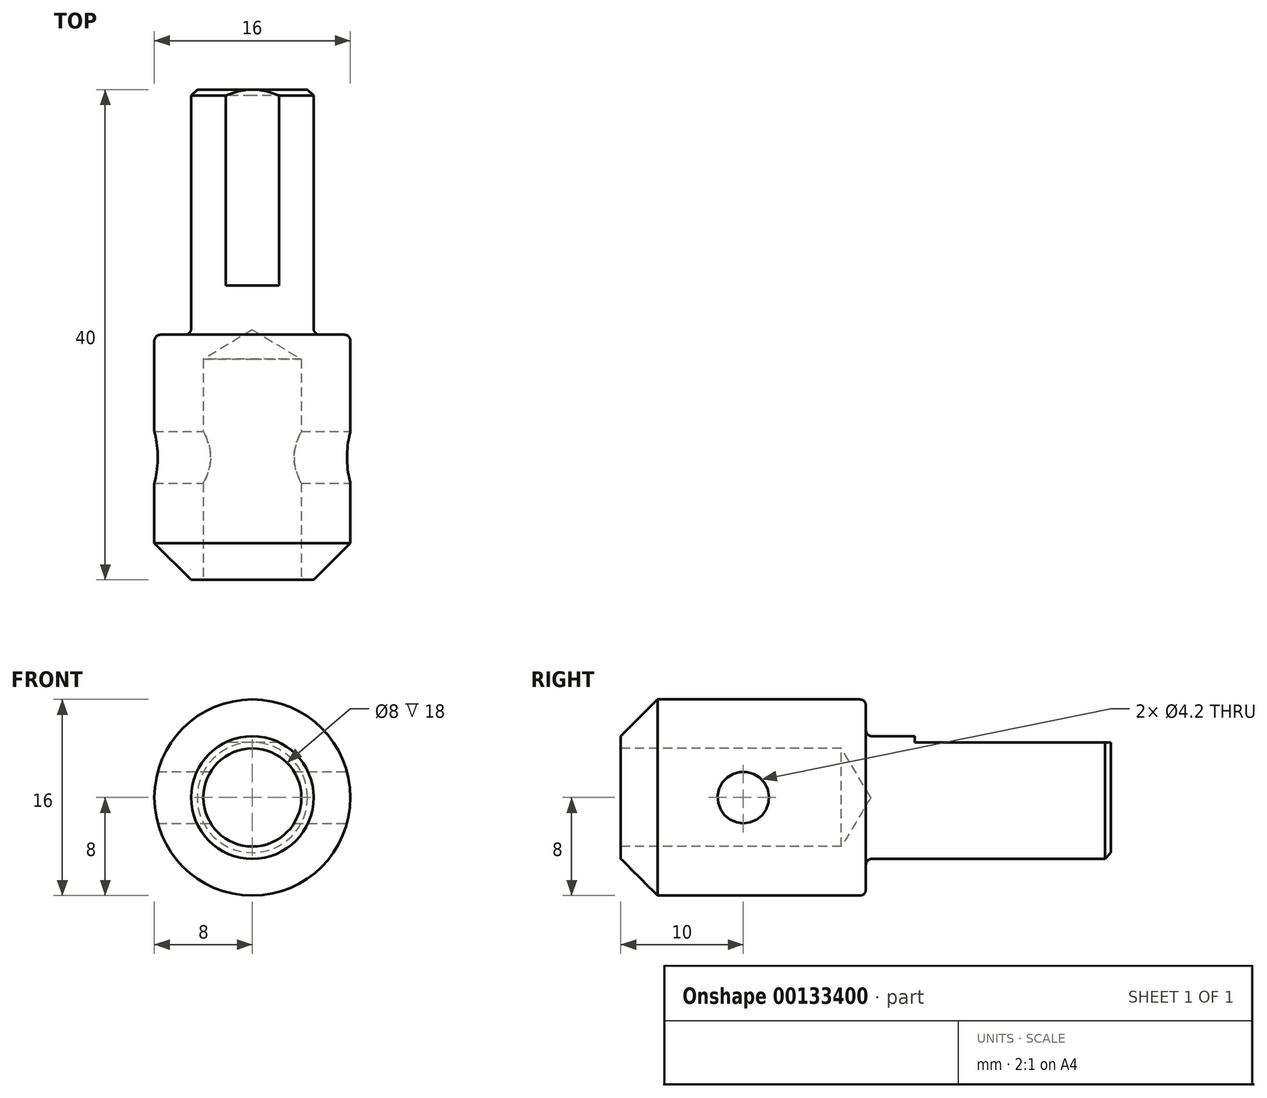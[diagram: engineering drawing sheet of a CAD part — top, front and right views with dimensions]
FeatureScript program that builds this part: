
annotation { "Feature Type Name" : "Feature", "Feature Type Description" : "" }
export const myFeature = defineFeature(function(context is Context, id is Id, definition is map)
    precondition{}
    {
        {
            var Q0;
            Q0=qCreatedBy(makeId("Front.planeOp"),FACE);
            var sketch = newSketch(context, id + "F0", { "sketchPlane" : qUnion([Q0])});
            skCircle(sketch, "E0", {"center": v(0, 0) * mm, "radius": 8 * mm});
            skSolve(sketch);
        }
        {
            var Q0;
            Q0=qSketchRegion(id+"F0",true);
            extrude(context, id + "F1", {"entities" : qUnion([Q0]), "oppositeDirection" : true, "depth" : 20 * mm});
        }
        {
            var Q0;
            Q0=makeQuery(id+"F1.opExtrude","CAP_FACE",FACE,{"disambiguationData":[OSD([sQuery(id+"F0.wireOp",EDGE,"E0")])],"isStart":false});
            var sketch = newSketch(context, id + "F2", { "sketchPlane" : qUnion([Q0])});
            skCircle(sketch, "E1", {"center": v(0, 0) * mm, "radius": 5 * mm});
            skSolve(sketch);
        }
        {
            var Q0;
            Q0=qSketchRegion(id+"F2",true);
            extrude(context, id + "F3", {"entities" : qUnion([Q0]), "operationType" : NewBodyOperationType.ADD, "depth" : 20 * mm});
        }
        {
            var Q0;
            Q0=makeQuery(id+"F3.opExtrude","CAP_FACE",FACE,{"disambiguationData":[OSD([sQuery(id+"F2.wireOp",EDGE,"E1")])],"isStart":false});
            var sketch = newSketch(context, id + "F4", { "sketchPlane" : qUnion([Q0])});
            skLineSegment(sketch, "E2", {"start": v(-2.18, 4.5) * mm, "end": v(2.18, 4.5) * mm});
            skArc(sketch, "E3", {"start": v(2.18, 4.5) * mm, "mid": v(0, 5) * mm, "end": v(-2.18, 4.5) * mm});
            skSolve(sketch);
        }
        {
            var Q0;
            Q0=qSketchRegion(id+"F4",true);
            extrude(context, id + "F5", {"entities" : qUnion([Q0]), "operationType" : NewBodyOperationType.REMOVE, "oppositeDirection" : true, "depth" : 16 * mm});
        }
        {
            var Q0;
            Q0=makeQuery(id+"F3.opExtrude","CAP_EDGE",EDGE,{"disambiguationData":[OSD([sQuery(id+"F2.wireOp",EDGE,"E1")])],"isStart":false});
            chamfer(context, id + "F6", {"entities" : qUnion([Q0]), "width" : .5 * mm, "tangentPropagation" : true});
        }
        {
            var Q0;
            Q0=makeQuery(id+"F1.opExtrude","CAP_FACE",FACE,{"disambiguationData":[OSD([sQuery(id+"F0.wireOp",EDGE,"E0")])],"isStart":false});
            fillet(context, id + "F7", {"entities" : qUnion([Q0]), "radius" : .5 * mm, "tangentPropagation" : true, "allowEdgeOverflow" : false});
        }
        {
            var Q0;
            Q0=makeQuery(id+"F1.opExtrude","CAP_FACE",FACE,{"disambiguationData":[OSD([sQuery(id+"F0.wireOp",EDGE,"E0")])],"isStart":true});
            var sketch = newSketch(context, id + "F8", { "sketchPlane" : qUnion([Q0])});
            skPoint(sketch, "E4", {"position": v(0, 0) * mm});
            skSolve(sketch);
        }
        {
            var Q0;
            Q0=sQuery(id+"F8.wireOp",VERTEX,"E4");
            var Q1;
            Q1=makeQuery(id+"F1.opExtrude","SWEPT_BODY",BODY,{"disambiguationData":[OSD([sQuery(id+"F0.wireOp",EDGE,"E0")])]});
            hole(context, id + "F9", {"style" : HoleStyle.SIMPLE, "endStyle" : HoleEndStyle.BLIND, "holeDiameter" : 8 * mm, "holeDepth" : 18 * mm, "locations" : qUnion([Q0]), "scope" : qUnion([Q1])});
        }
        {
            var Q0;
            Q0=qCreatedBy(makeId("Right.planeOp"),FACE);
            var sketch = newSketch(context, id + "F10", { "sketchPlane" : qUnion([Q0])});
            skCircle(sketch, "E5", {"center": v(10, 0) * mm, "radius": 2.1 * mm});
            skSolve(sketch);
        }
        {
            var Q0;
            Q0=qSketchRegion(id+"F10",true);
            extrude(context, id + "F11", {"entities" : qUnion([Q0]), "operationType" : NewBodyOperationType.REMOVE, "endBound" : BoundingType.SYMMETRIC, "oppositeDirection" : true, "depth" : 16.5 * mm});
        }
        {
            var Q0;
            Q0=makeQuery(id+"F1.opExtrude","CAP_EDGE",EDGE,{"disambiguationData":[OSD([sQuery(id+"F0.wireOp",EDGE,"E0")])],"isStart":true});
            chamfer(context, id + "F12", {"entities" : qUnion([Q0]), "width" : 3 * mm, "tangentPropagation" : true});
        }
    });
